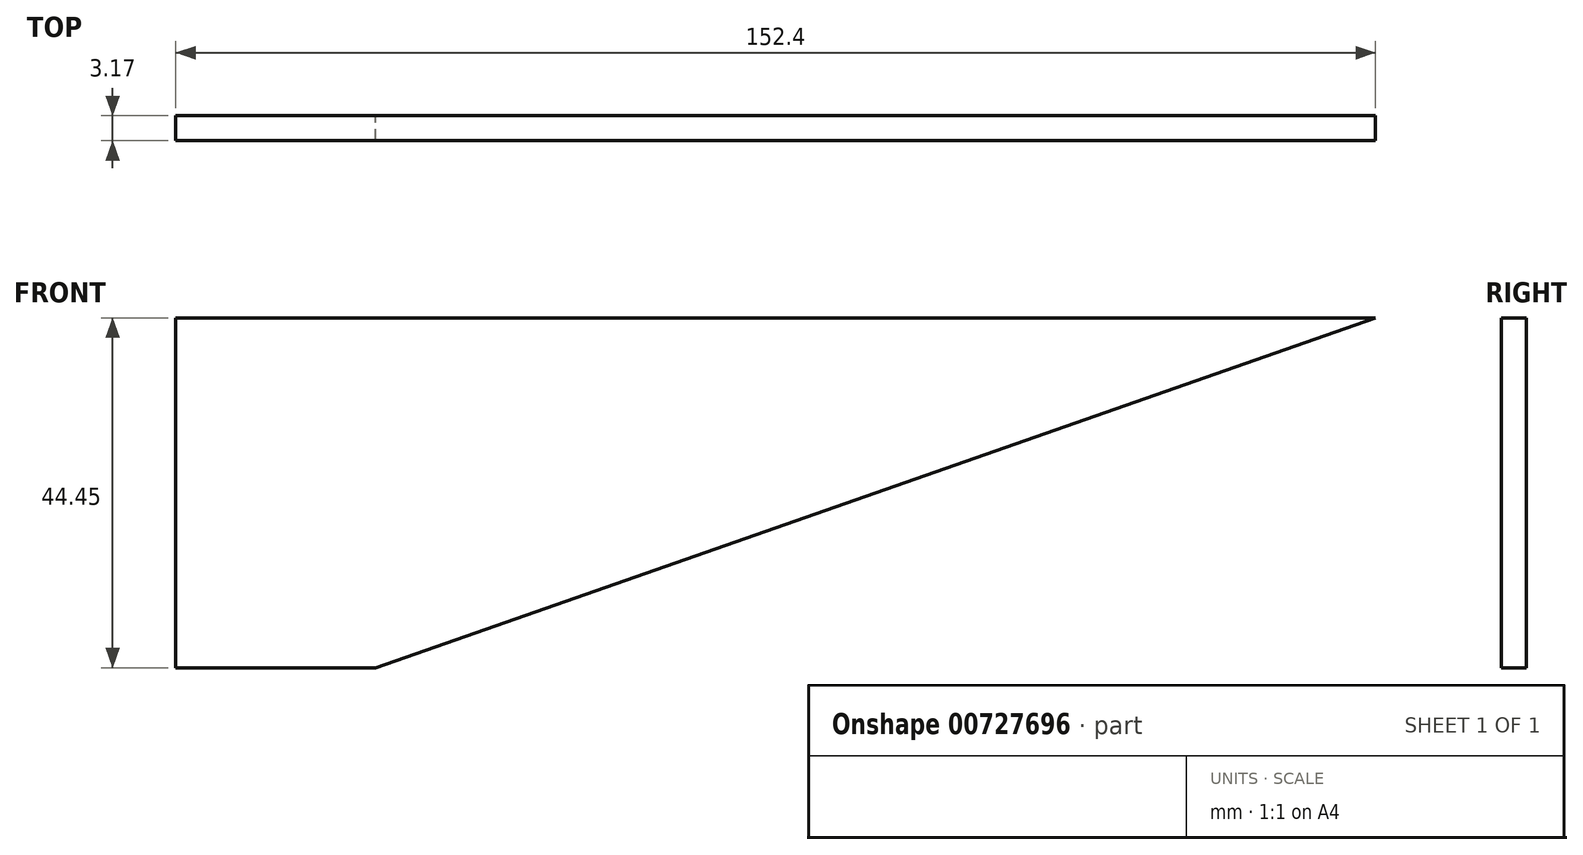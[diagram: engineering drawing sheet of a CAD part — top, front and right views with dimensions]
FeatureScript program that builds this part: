
annotation { "Feature Type Name" : "Feature", "Feature Type Description" : "" }
export const myFeature = defineFeature(function(context is Context, id is Id, definition is map)
    precondition{}
    {
        {
            var Q0;
            Q0=qCreatedBy(makeId("Front.planeOp"),FACE);
            var sketch = newSketch(context, id + "F0", { "sketchPlane" : qUnion([Q0])});
            skLineSegment(sketch, "E0", {"start": v(0, 0) * mm, "end": v(0, 44.45) * mm});
            skLineSegment(sketch, "E1", {"start": v(0, 44.45) * mm, "end": v(152.4, 44.45) * mm});
            skLineSegment(sketch, "E2", {"start": v(152.4, 44.45) * mm, "end": v(25.4, 0) * mm});
            skLineSegment(sketch, "E3", {"start": v(25.4, 0) * mm, "end": v(0, 0) * mm});
            skSolve(sketch);
        }
        {
            var Q0;
            Q0 = qSketchRegion(id + "F0", true);
            extrude(context, id + "F1", {"entities" : qUnion([Q0]), "depth" : 3.17 * mm, "offsetDistance" : 25.4 * mm});
        }
    });
